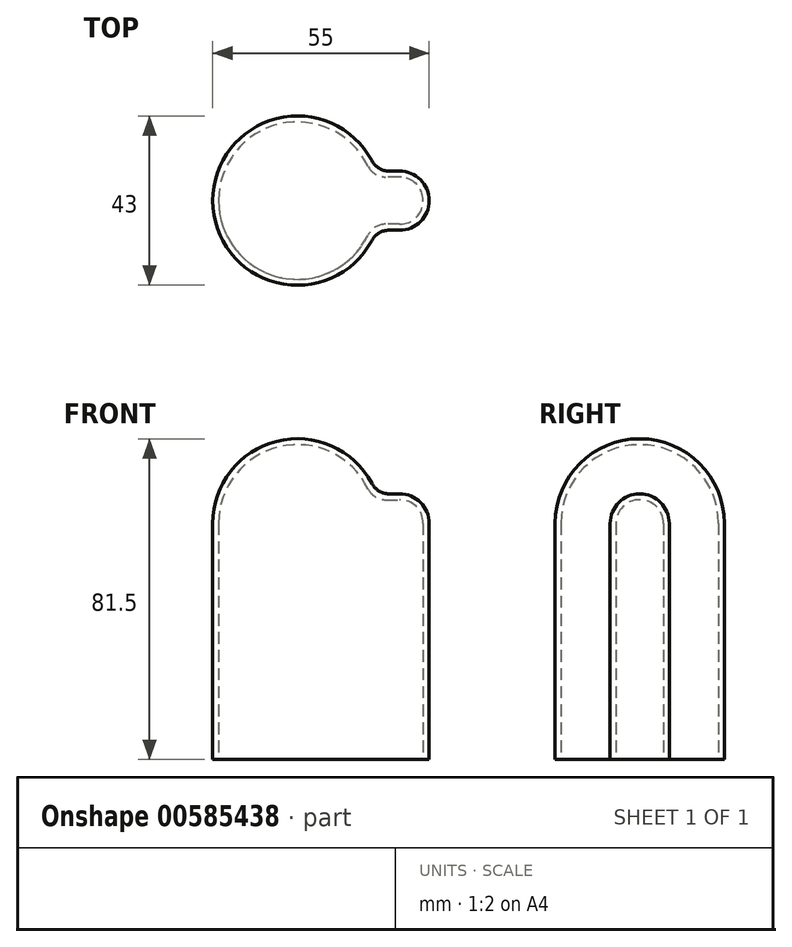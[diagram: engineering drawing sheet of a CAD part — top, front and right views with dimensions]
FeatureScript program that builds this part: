
annotation { "Feature Type Name" : "Feature", "Feature Type Description" : "" }
export const myFeature = defineFeature(function(context is Context, id is Id, definition is map)
    precondition{}
    {
        {
            var Q0;
            Q0=qCreatedBy(makeId("Top.planeOp"),FACE);
            var sketch = newSketch(context, id + "F0", { "sketchPlane" : qUnion([Q0])});
            skArc(sketch, "E0", {"start": v(17.96, 8.8) * mm, "mid": v(-20, 0) * mm, "end": v(17.96, -8.8) * mm});
            skLineSegment(sketch, "E1.bottom", {"start": v(26, 6) * mm, "end": v(22.45, 6) * mm});
            skLineSegment(sketch, "E1.top", {"start": v(26, -6) * mm, "end": v(22.45, -6) * mm});
            skPoint(sketch, "E1.middle", {"position": v(20, 0) * mm});
            skArc(sketch, "E2", {"start": v(26, -6) * mm, "mid": v(32, 0) * mm, "end": v(26, 6) * mm});
            skPoint(sketch, "E3.orphan", {"position": v(14, 6) * mm});
            skPoint(sketch, "E4.orphan", {"position": v(14, -6) * mm});
            skPoint(sketch, "E5.visualSharp", {"position": v(19.08, 6) * mm});
            skArc(sketch, "E5.filletArc", {"start": v(17.96, 8.8) * mm, "mid": v(19.8, 6.76) * mm, "end": v(22.45, 6) * mm});
            skPoint(sketch, "E6.visualSharp", {"position": v(19.08, -6) * mm});
            skArc(sketch, "E6.filletArc", {"start": v(22.45, -6) * mm, "mid": v(19.8, -6.76) * mm, "end": v(17.96, -8.8) * mm});
            skArc(sketch, "E7.0", {"start": v(18.96, 10.14) * mm, "mid": v(-21.5, 0) * mm, "end": v(18.96, -10.14) * mm});
            skLineSegment(sketch, "E7.1", {"start": v(26, 7.5) * mm, "end": v(23.37, 7.5) * mm});
            skArc(sketch, "E7.2", {"start": v(26, -7.5) * mm, "mid": v(33.5, 0) * mm, "end": v(26, 7.5) * mm});
            skLineSegment(sketch, "E7.3", {"start": v(26, -7.5) * mm, "end": v(23.37, -7.5) * mm});
            skPoint(sketch, "E8.visualSharp", {"position": v(20.15, -7.5) * mm});
            skArc(sketch, "E8.filletArc", {"start": v(23.37, -7.5) * mm, "mid": v(20.8, -8.21) * mm, "end": v(18.96, -10.14) * mm});
            skPoint(sketch, "E9.visualSharp", {"position": v(20.15, 7.5) * mm});
            skArc(sketch, "E9.filletArc", {"start": v(18.96, 10.14) * mm, "mid": v(20.8, 8.21) * mm, "end": v(23.37, 7.5) * mm});
            skSolve(sketch);
        }
        {
            var Q0;
            Q0=makeQuery(id+"F0.imprint","IMPRINT",FACE,{"disambiguationData":[TD([[makeQuery(id+"F0.imprint","IMPRINT",EDGE,{"derivedFrom":sQuery(id+"F0.wireOp",EDGE,"E0")}),-1.0]])]});
            extrude(context, id + "F1", {"entities" : qUnion([Q0]), "depth" : 60 * mm, "offsetDistance" : 25 * mm});
        }
        {
            var Q0;
            Q0=qCreatedBy(makeId("Top.planeOp"),FACE);
            cPlane(context, id + "F2", {"entities" : qUnion([Q0]), "cplaneType" : CPlaneType.OFFSET, "offset" : 60 * mm, "width" : 150 * mm, "height" : 150 * mm});
        }
        {
            var Q0;
            Q0=qCreatedBy(id+"F2.planeOp",FACE);
            var sketch = newSketch(context, id + "F3", { "sketchPlane" : qUnion([Q0])});
            skArc(sketch, "E10", {"start": v(-20, 0) * mm, "mid": v(-4.52, -19.48) * mm, "end": v(17.96, -8.8) * mm});
            skLineSegment(sketch, "E11.top", {"start": v(26, -6) * mm, "end": v(22.45, -6) * mm});
            skPoint(sketch, "E11.middle", {"position": v(20, 0) * mm});
            skArc(sketch, "E12", {"start": v(26, -6) * mm, "mid": v(30.24, -4.24) * mm, "end": v(32, 0) * mm});
            skPoint(sketch, "E13.orphan", {"position": v(14, -6) * mm});
            skPoint(sketch, "E14.visualSharp", {"position": v(19.08, -6) * mm});
            skArc(sketch, "E14.filletArc", {"start": v(22.45, -6) * mm, "mid": v(19.8, -6.76) * mm, "end": v(17.96, -8.8) * mm});
            skArc(sketch, "E15.0", {"start": v(-21.5, 0) * mm, "mid": v(-5.23, -20.85) * mm, "end": v(18.96, -10.14) * mm});
            skArc(sketch, "E15.2", {"start": v(26, -7.5) * mm, "mid": v(31.3, -5.3) * mm, "end": v(33.5, 0) * mm});
            skLineSegment(sketch, "E15.3", {"start": v(26, -7.5) * mm, "end": v(23.37, -7.5) * mm});
            skPoint(sketch, "E16.visualSharp", {"position": v(20.15, -7.5) * mm});
            skArc(sketch, "E16.filletArc", {"start": v(23.37, -7.5) * mm, "mid": v(20.8, -8.21) * mm, "end": v(18.96, -10.14) * mm});
            skLineSegment(sketch, "E17", {"start": v(-21.5, 0) * mm, "end": v(33.5, 0) * mm});
            skSolve(sketch);
        }
        {
            var Q0;
            {var subQ1=sQuery(id+"F3.wireOp",EDGE,"E10");Q0=makeQuery(id+"F3.imprint","IMPRINT",FACE,{"disambiguationData":[TD([[makeQuery(id+"F3.imprint","IMPRINT",EDGE,{"derivedFrom":subQ1}),-1.0]])]});}
            var Q1;
            Q1=sQuery(id+"F3.wireOp",EDGE,"E17");
            revolve(context, id + "F4", {"operationType" : NewBodyOperationType.ADD, "entities" : qUnion([Q0]), "axis" : qUnion([Q1]), "revolveType" : RevolveType.ONE_DIRECTION, "oppositeDirection" : true, "angle" : 180 * degree});
        }
    });
